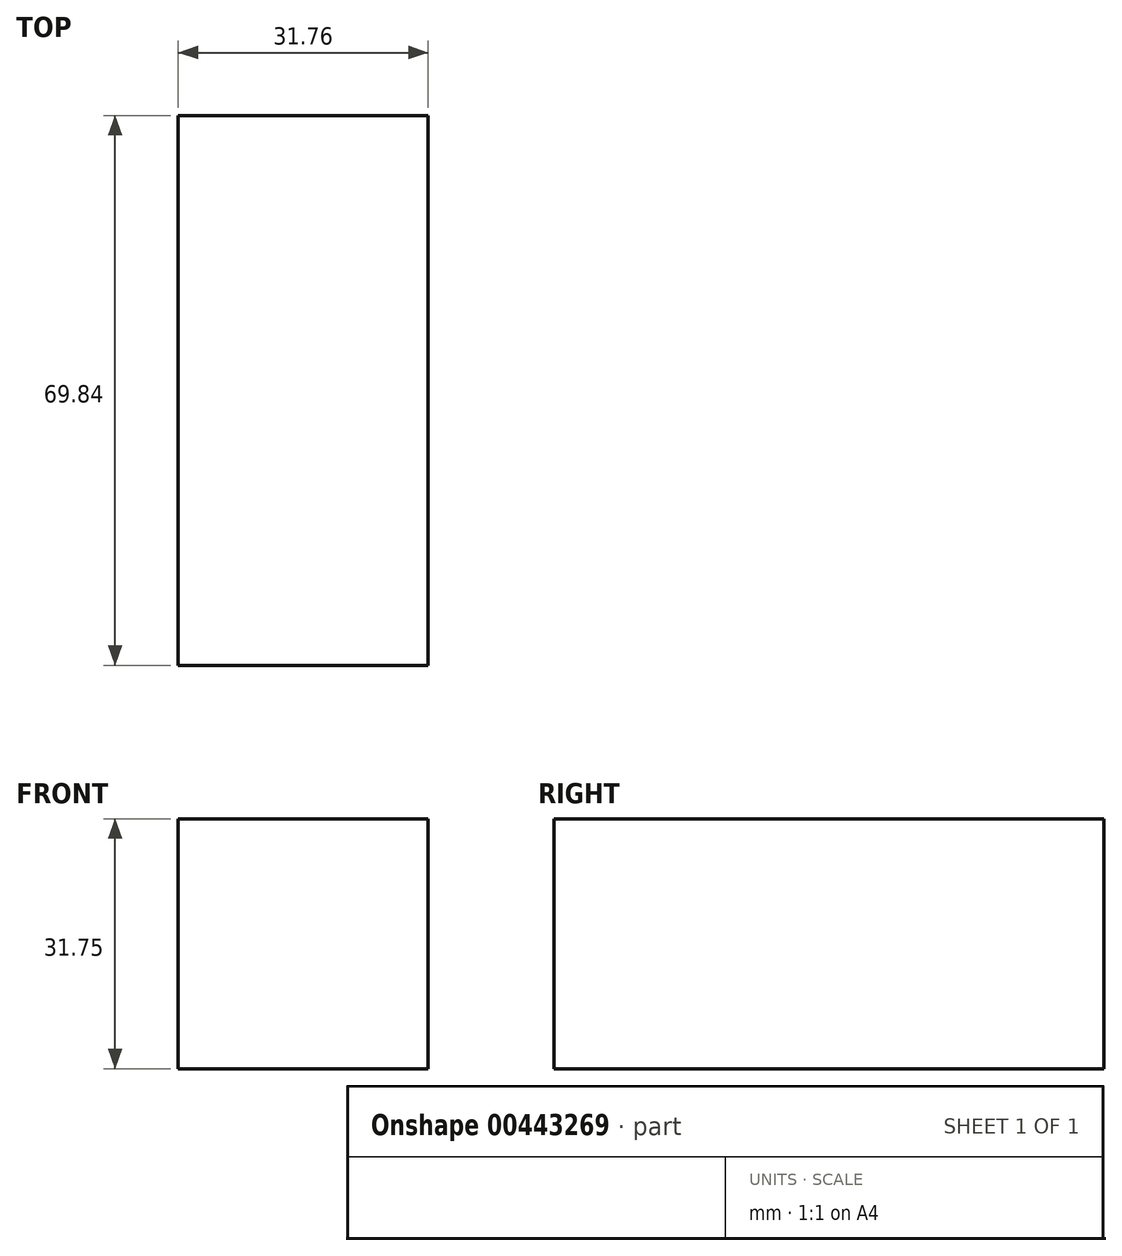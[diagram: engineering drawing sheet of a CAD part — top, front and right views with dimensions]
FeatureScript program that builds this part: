
annotation { "Feature Type Name" : "Feature", "Feature Type Description" : "" }
export const myFeature = defineFeature(function(context is Context, id is Id, definition is map)
    precondition{}
    {
        {
            var Q0;
            Q0=qCreatedBy(makeId("Top.planeOp"),FACE);
            var sketch = newSketch(context, id + "F0", { "sketchPlane" : qUnion([Q0])});
            skLineSegment(sketch, "E0.bottom", {"start": v(15.88, -34.93) * mm, "end": v(-15.87, -34.93) * mm});
            skLineSegment(sketch, "E0.top", {"start": v(15.87, 34.93) * mm, "end": v(-15.87, 34.93) * mm});
            skLineSegment(sketch, "E0.left", {"start": v(15.88, -34.93) * mm, "end": v(15.88, 34.92) * mm});
            skLineSegment(sketch, "E0.right", {"start": v(-15.87, -34.93) * mm, "end": v(-15.87, 34.92) * mm});
            skPoint(sketch, "E0.middle", {"position": v(0, 0) * mm});
            skSolve(sketch);
        }
        {
            var Q0;
            Q0=makeQuery(id+"F0.imprint","IMPRINT",FACE,{"disambiguationData":[TD([[makeQuery(id+"F0.imprint","IMPRINT",EDGE,{"derivedFrom":sQuery(id+"F0.wireOp",EDGE,"E0.bottom")}),-1.0]])]});
            extrude(context, id + "F1", {"entities" : qUnion([Q0]), "depth" : 31.75 * mm});
        }
    });
